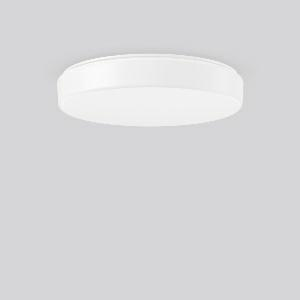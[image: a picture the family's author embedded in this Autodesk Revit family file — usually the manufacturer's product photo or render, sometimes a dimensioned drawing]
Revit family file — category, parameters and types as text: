
# Revit family: flat_polymero_kreis_672392_002_89_1398
name_source: partatom
category: Lighting Fixtures
units: mm (PartAtom-declared; Revit-internal decimal feet)

## family parameters
Cut with Voids When Loaded = No
Host = Face
Light Source = No
Part Type = Normal
Room Calculation Point = No
Round Connector Dimension = Use Diameter
Shared = No

## types (1)
- FLAT POLYMERO KREIS (1 x LED Modul 830, 2500 lm, 3000)
    Apparent Load = 24 VA
    CIE Flux Codes = 42 72 91 84 100
    Color Rendering = 80
    Color Temperature = 3000
    Default Elevation = 1800 mm
    Description = Series: FLAT POLYMERO KREIS
Decorative round surface-mounted luminaire. For escape route illumination. Base: metal, powder-coated. Diffuser made of non-yellowing plastic (PMMA), opal. Diffuser fastening: patented push system. Suitable for Ceiling mounting, Wall (surface). Driver integrated. Suitable for connection to central battery systems. With AC Control monitoring module for LUXIFAIR central battery units. 
Colour: white
Diameter: 515 mm
Height: 98 mm
Weight: 2.86 kg
Operating mode: Non-maintained power mode and maintained power mode
Lamp: LED
Socket: without socket
Colour temperature: 3000K
Colour rendering index (CRI): 80
System power: 24 W
Rated luminous flux: 2500 lm
Luminous flux, emergency: 520 lm
System power, emergency: 6.9 W
Control gear: Regulated power supply
Protection class: I
Type of protection: IP 40
    Height = 98 mm
    Lamp = 1 x LED Modul 830
    Lamp Light Flux = 2500 lm
    Lamp count = 1
    Length = 515 mm
    Lifetime = 50000 h
    Luminous efficacy = 104 lm/W
    Manufacturer = RZB
    ModVariant = No
    Model = 672392.002.89
    Mounting Place = Ceiling, Wall
    Mounting Type = Surface mounted
    Number of Poles = 1
    OnlyDefault = Yes
    Power Factor = 1
    Product Name = FLAT POLYMERO KREIS
    Product group = Surface mounted ceiling and wall luminaires
    ProductGroupID = 305
    Protection Class = Protection class I
    Protection Degree = IP 40
    RLX_Detail_Level = 1
    RLX_Emergency_Light_Flux = 520 lm
    RLX_Emergency_Type = 3
    RLX_Emergency_Type_DB = Yes
    RlxData = <blob elided: 57101 chars, md5=cc8a4e16>
    Socket = socket
    Standby Power = 0 W
    System Light Flux = 2500 lm
    System Power = 24 W
    Type Comments = Product without accessories
    Type Image = 311604.862.79.jpg
    URL = http://relux.com
    VarID = ---
    Voltage = 230 V
    Voltage Range = 220-240 V
    Weight = 0.00 kg
    Width = 0 mm  [stored 0 ft]

note: [stored X ft] marks values corroborated as IEEE doubles in the binary element streams (Revit-internal decimal feet)

## geometry (parser evidence)
native form markers: Blend x4, Sweep x17
no freeform markers — native parametric forms only
